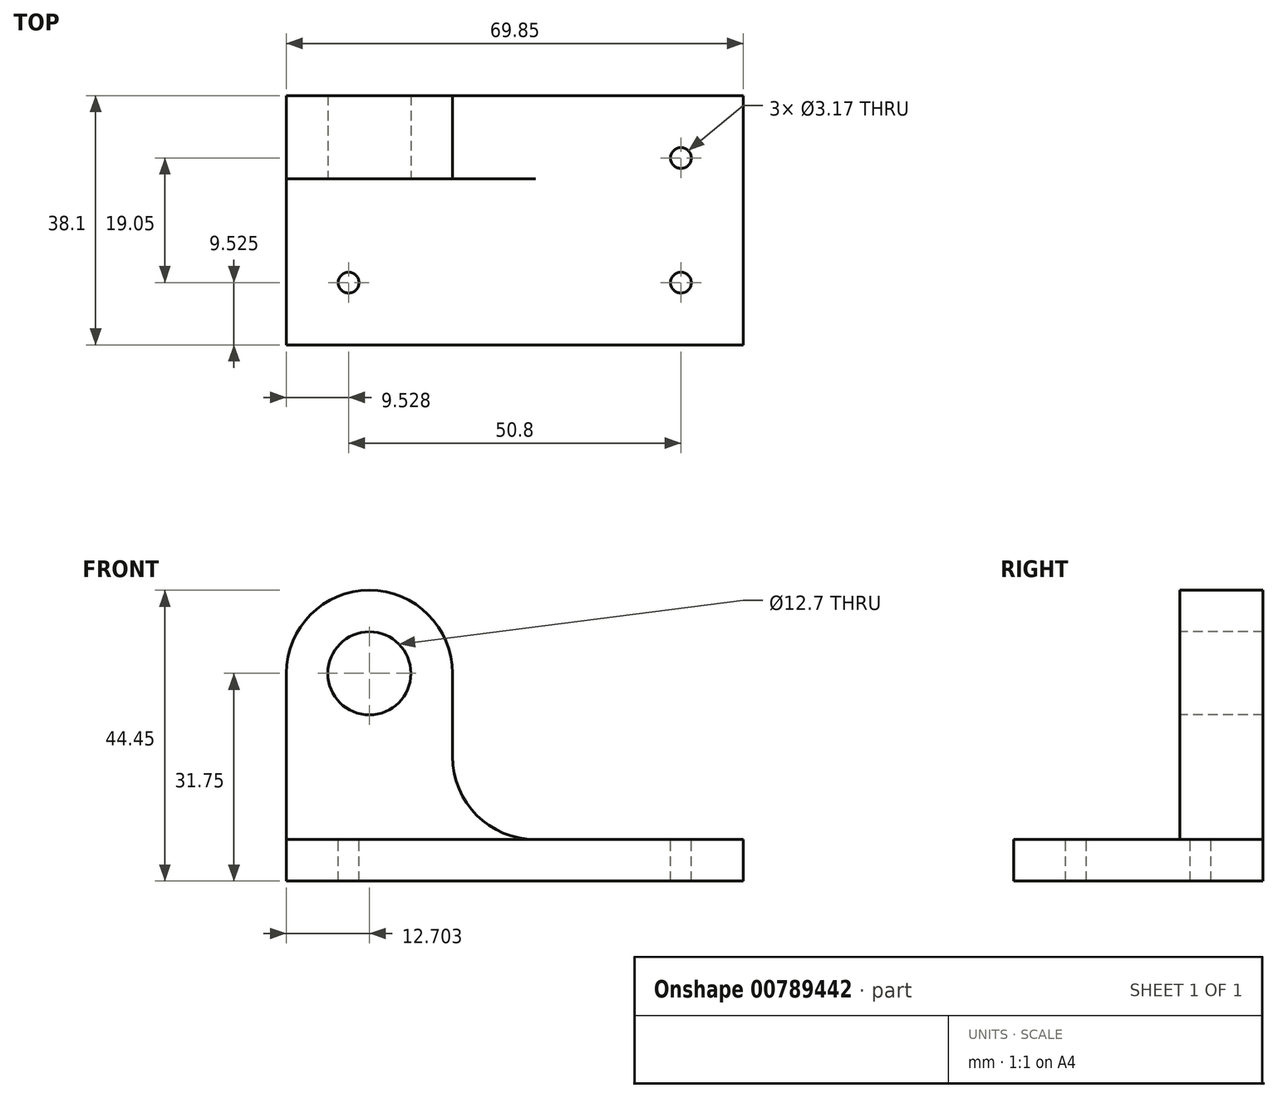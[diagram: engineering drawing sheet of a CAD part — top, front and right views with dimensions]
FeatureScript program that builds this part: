
annotation { "Feature Type Name" : "Feature", "Feature Type Description" : "" }
export const myFeature = defineFeature(function(context is Context, id is Id, definition is map)
    precondition{}
    {
        {
            var Q0;
            Q0=qCreatedBy(makeId("Front.planeOp"),FACE);
            var sketch = newSketch(context, id + "F0", { "sketchPlane" : qUnion([Q0])});
            skLineSegment(sketch, "E0", {"start": v(-42.86, 44.45) * mm, "end": v(-42.86, 0) * mm});
            skLineSegment(sketch, "E1", {"start": v(-42.86, 0) * mm, "end": v(27, 0) * mm});
            skLineSegment(sketch, "E2", {"start": v(-42.86, 44.45) * mm, "end": v(-17.46, 44.45) * mm});
            skLineSegment(sketch, "E3", {"start": v(-17.46, 44.45) * mm, "end": v(-17.46, 6.35) * mm});
            skLineSegment(sketch, "E4", {"start": v(-17.46, 6.35) * mm, "end": v(27, 6.35) * mm});
            skLineSegment(sketch, "E5", {"start": v(27, 6.35) * mm, "end": v(27, 0) * mm});
            skSolve(sketch);
        }
        {
            var Q0;
            Q0=makeQuery(id+"F0.imprint","IMPRINT",FACE,{"disambiguationData":[TD([[makeQuery(id+"F0.imprint","IMPRINT",EDGE,{"derivedFrom":sQuery(id+"F0.wireOp",EDGE,"E0")}),1.0]])]});
            extrude(context, id + "F1", {"entities" : qUnion([Q0]), "depth" : 38.1 * mm, "offsetDistance" : 25.4 * mm});
        }
        {
            var Q0;
            Q0=makeQuery(id+"F1.opExtrude","CAP_FACE",FACE,{"disambiguationData":[OSD([sQuery(id+"F0.wireOp",EDGE,"E0"),sQuery(id+"F0.wireOp",EDGE,"E1"),sQuery(id+"F0.wireOp",EDGE,"E2"),sQuery(id+"F0.wireOp",EDGE,"E3"),sQuery(id+"F0.wireOp",EDGE,"E4"),sQuery(id+"F0.wireOp",EDGE,"E5")])],"isStart":false});
            var sketch = newSketch(context, id + "F2", { "sketchPlane" : qUnion([Q0])});
            skLineSegment(sketch, "E6", {"start": v(-17.46, 6.35) * mm, "end": v(-42.86, 6.35) * mm});
            skLineSegment(sketch, "E7", {"start": v(-42.86, 6.35) * mm, "end": v(-42.86, 44.45) * mm});
            skLineSegment(sketch, "E8", {"start": v(-42.86, 44.45) * mm, "end": v(-17.46, 44.45) * mm});
            skLineSegment(sketch, "E9", {"start": v(-17.46, 44.45) * mm, "end": v(-17.46, 6.35) * mm});
            skSolve(sketch);
        }
        {
            var Q0;
            Q0=makeQuery(id+"F2.imprint","IMPRINT",FACE,{"disambiguationData":[TD([[makeQuery(id+"F2.imprint","IMPRINT",EDGE,{"derivedFrom":sQuery(id+"F2.wireOp",EDGE,"E6")}),-1.0]])]});
            extrude(context, id + "F3", {"entities" : qUnion([Q0]), "operationType" : NewBodyOperationType.REMOVE, "oppositeDirection" : true, "depth" : 25.4 * mm, "offsetDistance" : 25.4 * mm});
        }
        {
            var Q0;
            Q0=makeQuery(id+"F3.boolean.opBoolean","COPY",FACE,{"derivedFrom":makeQuery(id+"F3.opExtrude","CAP_FACE",FACE,{"disambiguationData":[OSD([sQuery(id+"F2.wireOp",EDGE,"E6"),sQuery(id+"F2.wireOp",EDGE,"E7"),sQuery(id+"F2.wireOp",EDGE,"E8"),sQuery(id+"F2.wireOp",EDGE,"E9")])],"isStart":false})});
            var sketch = newSketch(context, id + "F4", { "sketchPlane" : qUnion([Q0])});
            skCircle(sketch, "E10", {"center": v(-30.16, 31.75) * mm, "radius": 6.35 * mm});
            skSolve(sketch);
        }
        {
            var Q0;
            Q0=makeQuery(id+"F4.imprint","IMPRINT",FACE,{"disambiguationData":[TD([[makeQuery(id+"F4.imprint","IMPRINT",EDGE,{"derivedFrom":sQuery(id+"F4.wireOp",EDGE,"E10")}),1.0]])]});
            extrude(context, id + "F5", {"entities" : qUnion([Q0]), "operationType" : NewBodyOperationType.REMOVE, "oppositeDirection" : true, "depth" : 12.7 * mm, "offsetDistance" : 25.4 * mm});
        }
        {
            var Q0;
            Q0=makeQuery(id+"F3.boolean.opBoolean","COPY",FACE,{"derivedFrom":makeQuery(id+"F3.opExtrude","CAP_FACE",FACE,{"disambiguationData":[OSD([sQuery(id+"F2.wireOp",EDGE,"E6"),sQuery(id+"F2.wireOp",EDGE,"E7"),sQuery(id+"F2.wireOp",EDGE,"E8"),sQuery(id+"F2.wireOp",EDGE,"E9")])],"isStart":false})});
            var sketch = newSketch(context, id + "F6", { "sketchPlane" : qUnion([Q0])});
            skArc(sketch, "E11", {"start": v(-30.16, 44.45) * mm, "mid": v(-39.14, 40.73) * mm, "end": v(-42.86, 31.75) * mm});
            skArc(sketch, "E12", {"start": v(-17.46, 31.75) * mm, "mid": v(-21.18, 40.73) * mm, "end": v(-30.16, 44.45) * mm});
            skSolve(sketch);
        }
        {
            var Q0;
            {var subQ0=sQuery(id+"F6.wireOp",EDGE,"E11");Q0=makeQuery(id+"F6.imprint","IMPRINT",FACE,{"disambiguationData":[TD([[makeQuery(id+"F6.imprint","IMPRINT",EDGE,{"derivedFrom":subQ0}),-1.0]])]});}
            var Q1;
            {var subQ0=sQuery(id+"F6.wireOp",EDGE,"E12");Q1=makeQuery(id+"F6.imprint","IMPRINT",FACE,{"disambiguationData":[TD([[makeQuery(id+"F6.imprint","IMPRINT",EDGE,{"derivedFrom":subQ0}),-1.0]])]});}
            extrude(context, id + "F7", {"entities" : qUnion([Q0, Q1]), "operationType" : NewBodyOperationType.REMOVE, "oppositeDirection" : true, "depth" : 12.7 * mm, "offsetDistance" : 25.4 * mm});
        }
        {
            var Q0;
            Q0=makeQuery(id+"F3.boolean.opBoolean","COPY",FACE,{"derivedFrom":makeQuery(id+"F3.opExtrude","CAP_FACE",FACE,{"disambiguationData":[OSD([sQuery(id+"F2.wireOp",EDGE,"E6"),sQuery(id+"F2.wireOp",EDGE,"E7"),sQuery(id+"F2.wireOp",EDGE,"E8"),sQuery(id+"F2.wireOp",EDGE,"E9")])],"isStart":false})});
            var sketch = newSketch(context, id + "F8", { "sketchPlane" : qUnion([Q0])});
            skLineSegment(sketch, "E13", {"start": v(-17.46, 19.05) * mm, "end": v(-17.46, 6.35) * mm});
            skLineSegment(sketch, "E14", {"start": v(-17.46, 6.35) * mm, "end": v(-4.76, 6.35) * mm});
            skLineSegment(sketch, "E15", {"start": v(-17.46, 19.05) * mm, "end": v(-4.76, 19.05) * mm});
            skLineSegment(sketch, "E16", {"start": v(-4.76, 19.05) * mm, "end": v(-4.76, 6.35) * mm});
            skSolve(sketch);
        }
        {
            var Q0;
            Q0=makeQuery(id+"F8.imprint","IMPRINT",FACE,{"disambiguationData":[TD([[makeQuery(id+"F8.imprint","IMPRINT",EDGE,{"derivedFrom":sQuery(id+"F8.wireOp",EDGE,"E13")}),1.0]])]});
            extrude(context, id + "F9", {"entities" : qUnion([Q0]), "operationType" : NewBodyOperationType.ADD, "oppositeDirection" : true, "depth" : 12.7 * mm, "offsetDistance" : 25.4 * mm});
        }
        {
            var Q0;
            Q0=makeQuery(id+"F9.boolean.opBoolean","MERGE",FACE,{"derivedFrom":[makeQuery(id+"F3.boolean.opBoolean","COPY",FACE,{"derivedFrom":makeQuery(id+"F3.opExtrude","CAP_FACE",FACE,{"disambiguationData":[OSD([sQuery(id+"F2.wireOp",EDGE,"E6"),sQuery(id+"F2.wireOp",EDGE,"E7"),sQuery(id+"F2.wireOp",EDGE,"E8"),sQuery(id+"F2.wireOp",EDGE,"E9")])],"isStart":false})}),makeQuery(id+"F9.opExtrude","CAP_FACE",FACE,{"disambiguationData":[OSD([sQuery(id+"F8.wireOp",EDGE,"E13"),sQuery(id+"F8.wireOp",EDGE,"E14"),sQuery(id+"F8.wireOp",EDGE,"E15"),sQuery(id+"F8.wireOp",EDGE,"E16")])],"isStart":true})]});
            var sketch = newSketch(context, id + "F10", { "sketchPlane" : qUnion([Q0])});
            skArc(sketch, "E17", {"start": v(-17.46, 19.05) * mm, "mid": v(-13.74, 10.07) * mm, "end": v(-4.76, 6.35) * mm});
            skSolve(sketch);
        }
        {
            var Q0;
            Q0=makeQuery(id+"F10.imprint","IMPRINT",FACE,{"disambiguationData":[TD([[makeQuery(id+"F10.imprint","IMPRINT",EDGE,{"derivedFrom":sQuery(id+"F10.wireOp",EDGE,"E17")}),1.0]])]});
            extrude(context, id + "F11", {"entities" : qUnion([Q0]), "operationType" : NewBodyOperationType.REMOVE, "oppositeDirection" : true, "depth" : 12.7 * mm, "offsetDistance" : 25.4 * mm});
        }
        {
            var Q0;
            Q0=makeQuery(id+"F3.boolean.opBoolean","MERGE",FACE,{"derivedFrom":[makeQuery(id+"F1.opExtrude","SWEPT_FACE",FACE,{"disambiguationData":[OSD([sQuery(id+"F0.wireOp",EDGE,"E4")])]}),makeQuery(id+"F3.opExtrude","SWEPT_FACE",FACE,{"disambiguationData":[OSD([sQuery(id+"F2.wireOp",EDGE,"E6")])]})]});
            var sketch = newSketch(context, id + "F12", { "sketchPlane" : qUnion([Q0])});
            skCircle(sketch, "E18", {"center": v(-33.33, -28.57) * mm, "radius": 1.59 * mm});
            skCircle(sketch, "E19", {"center": v(17.47, -9.52) * mm, "radius": 1.59 * mm});
            skCircle(sketch, "E20", {"center": v(17.47, -28.58) * mm, "radius": 1.59 * mm});
            skSolve(sketch);
        }
        {
            var Q0;
            Q0=makeQuery(id+"F12.imprint","IMPRINT",FACE,{"disambiguationData":[TD([[makeQuery(id+"F12.imprint","IMPRINT",EDGE,{"derivedFrom":sQuery(id+"F12.wireOp",EDGE,"E18")}),1.0]])]});
            var Q1;
            Q1=makeQuery(id+"F12.imprint","IMPRINT",FACE,{"disambiguationData":[TD([[makeQuery(id+"F12.imprint","IMPRINT",EDGE,{"derivedFrom":sQuery(id+"F12.wireOp",EDGE,"E20")}),1.0]])]});
            var Q2;
            Q2=makeQuery(id+"F12.imprint","IMPRINT",FACE,{"disambiguationData":[TD([[makeQuery(id+"F12.imprint","IMPRINT",EDGE,{"derivedFrom":sQuery(id+"F12.wireOp",EDGE,"E19")}),1.0]])]});
            extrude(context, id + "F13", {"entities" : qUnion([Q0, Q1, Q2]), "operationType" : NewBodyOperationType.REMOVE, "oppositeDirection" : true, "depth" : 6.35 * mm});
        }
    });
